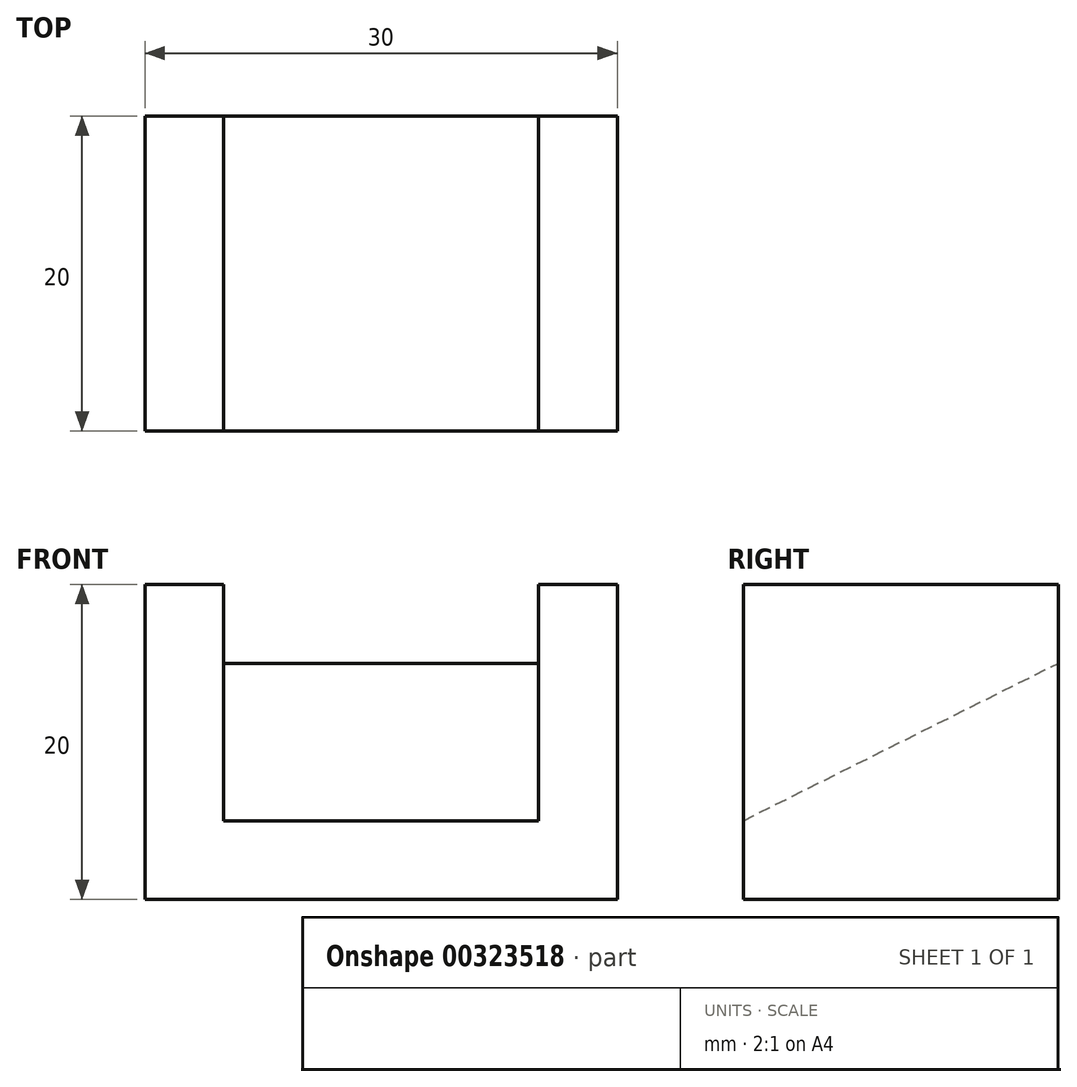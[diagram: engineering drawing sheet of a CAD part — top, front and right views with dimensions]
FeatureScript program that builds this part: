
annotation { "Feature Type Name" : "Feature", "Feature Type Description" : "" }
export const myFeature = defineFeature(function(context is Context, id is Id, definition is map)
    precondition{}
    {
        {
            var Q0;
            Q0=qCreatedBy(makeId("Front.planeOp"),FACE);
            var sketch = newSketch(context, id + "F0", { "sketchPlane" : qUnion([Q0])});
            skLineSegment(sketch, "E0", {"start": v(15, 0) * mm, "end": v(15, 20) * mm});
            skLineSegment(sketch, "E1", {"start": v(15, 20) * mm, "end": v(10, 20) * mm});
            skLineSegment(sketch, "E2", {"start": v(10, 20) * mm, "end": v(10, 5) * mm});
            skLineSegment(sketch, "E3", {"start": v(10, 5) * mm, "end": v(-10, 5) * mm});
            skLineSegment(sketch, "E4.MirrorCS", {"start": v(-15, 20) * mm, "end": v(-10, 20) * mm});
            skLineSegment(sketch, "E5.MirrorCS", {"start": v(-15, 0) * mm, "end": v(-15, 20) * mm});
            skLineSegment(sketch, "E6.MirrorCS", {"start": v(-10, 20) * mm, "end": v(-10, 5) * mm});
            skLineSegment(sketch, "E7", {"start": v(15, 0) * mm, "end": v(-15, 0) * mm});
            skSolve(sketch);
        }
        {
            var Q0;
            Q0=makeQuery(id+"F0.imprint","IMPRINT",FACE,{"disambiguationData":[TD([[makeQuery(id+"F0.imprint","IMPRINT",EDGE,{"derivedFrom":sQuery(id+"F0.wireOp",EDGE,"E0")}),1.0]])]});
            extrude(context, id + "F1", {"entities" : qUnion([Q0]), "depth" : 20 * mm, "symmetric" : true});
        }
        {
            var Q0;
            Q0=qCreatedBy(makeId("Right.planeOp"),FACE);
            var sketch = newSketch(context, id + "F2", { "sketchPlane" : qUnion([Q0])});
            skLineSegment(sketch, "E8.0.0", {"start": v(10, 0) * mm, "end": v(10, 20) * mm});
            skLineSegment(sketch, "E8.0.1", {"start": v(10, 20) * mm, "end": v(-10, 20) * mm});
            skLineSegment(sketch, "E8.0.2", {"start": v(-10, 20) * mm, "end": v(-10, 0) * mm});
            skLineSegment(sketch, "E8.0.3", {"start": v(-10, 0) * mm, "end": v(10, 0) * mm});
            skLineSegment(sketch, "E9", {"start": v(-10, 0) * mm, "end": v(-10, 5) * mm});
            skLineSegment(sketch, "E10", {"start": v(-10, 5) * mm, "end": v(10, 5) * mm});
            skLineSegment(sketch, "E11", {"start": v(10, 5) * mm, "end": v(10, 0) * mm});
            skLineSegment(sketch, "E12", {"start": v(-10, 5) * mm, "end": v(10, 15) * mm});
            skLineSegment(sketch, "E13", {"start": v(10, 15) * mm, "end": v(10, 5) * mm});
            skSolve(sketch);
        }
        {
            var Q0;
            Q0=makeQuery(id+"F2.imprint","IMPRINT",FACE,{"disambiguationData":[TD([[makeQuery(id+"F2.imprint","IMPRINT",EDGE,{"derivedFrom":sQuery(id+"F2.wireOp",EDGE,"E10")}),1.0]])]});
            extrude(context, id + "F3", {"entities" : qUnion([Q0]), "operationType" : NewBodyOperationType.ADD, "depth" : 20 * mm, "symmetric" : true});
        }
    });
